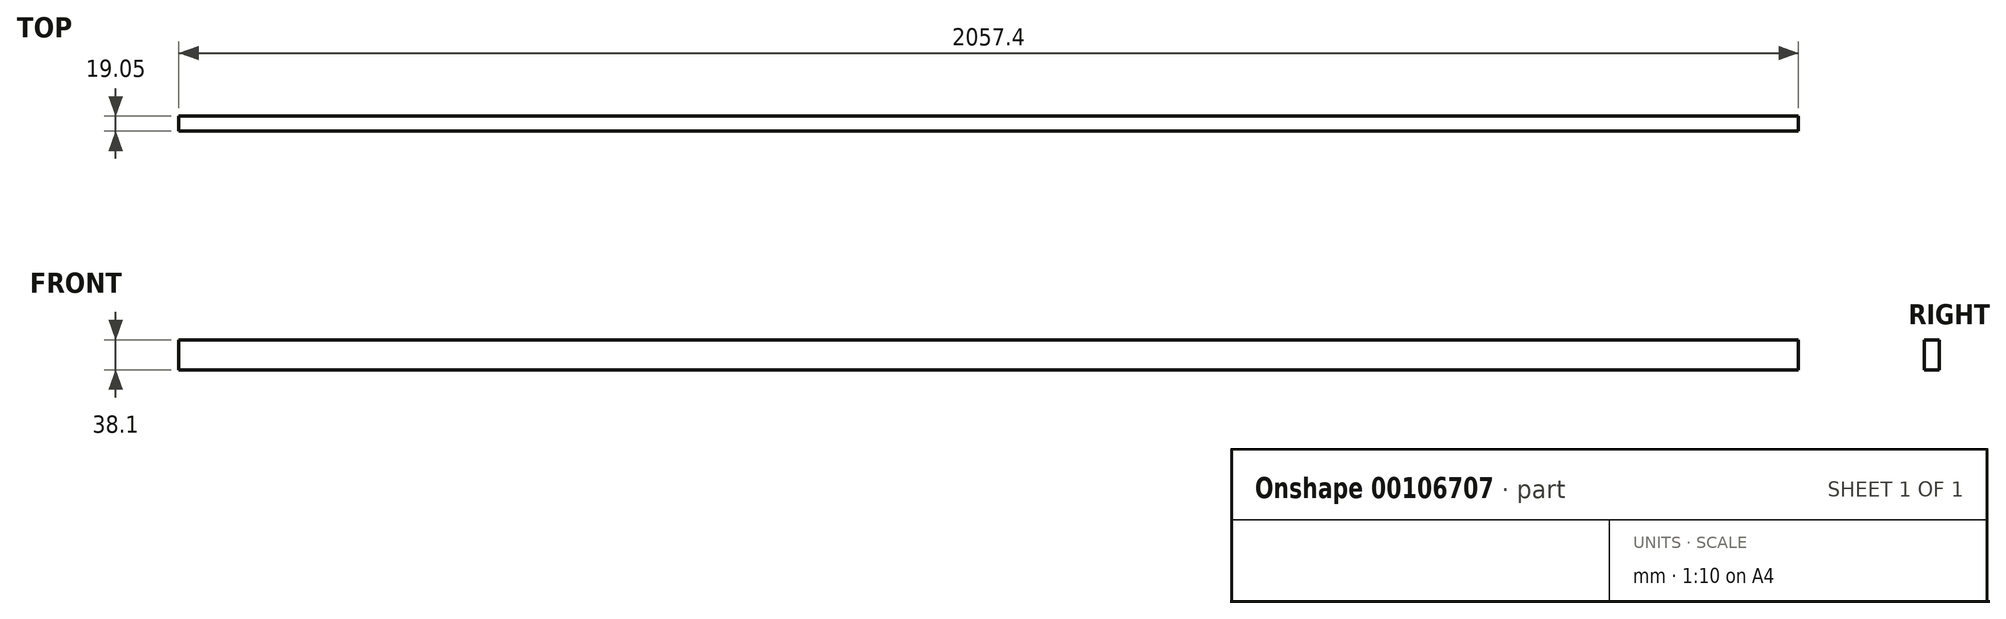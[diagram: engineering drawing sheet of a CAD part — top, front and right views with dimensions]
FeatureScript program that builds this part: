
annotation { "Feature Type Name" : "Feature", "Feature Type Description" : "" }
export const myFeature = defineFeature(function(context is Context, id is Id, definition is map)
    precondition{}
    {
        {
            var Q0;
            Q0=qCreatedBy(makeId("Front.planeOp"),FACE);
            var sketch = newSketch(context, id + "F0", { "sketchPlane" : qUnion([Q0])});
            skLineSegment(sketch, "E0.bottom", {"start": v(0, 0) * mm, "end": v(2057.4, 0) * mm});
            skLineSegment(sketch, "E0.top", {"start": v(0, 38.1) * mm, "end": v(2057.4, 38.1) * mm});
            skLineSegment(sketch, "E0.left", {"start": v(0, 0) * mm, "end": v(0, 38.1) * mm});
            skLineSegment(sketch, "E0.right", {"start": v(2057.4, 0) * mm, "end": v(2057.4, 38.1) * mm});
            skSolve(sketch);
        }
        {
            var Q0;
            Q0=makeQuery(id+"F0.imprint","IMPRINT",FACE,{"disambiguationData":[TD([[makeQuery(id+"F0.imprint","IMPRINT",EDGE,{"derivedFrom":sQuery(id+"F0.wireOp",EDGE,"E0.bottom")}),1.0]])]});
            extrude(context, id + "F1", {"entities" : qUnion([Q0]), "depth" : 19.05 * mm});
        }
    });
